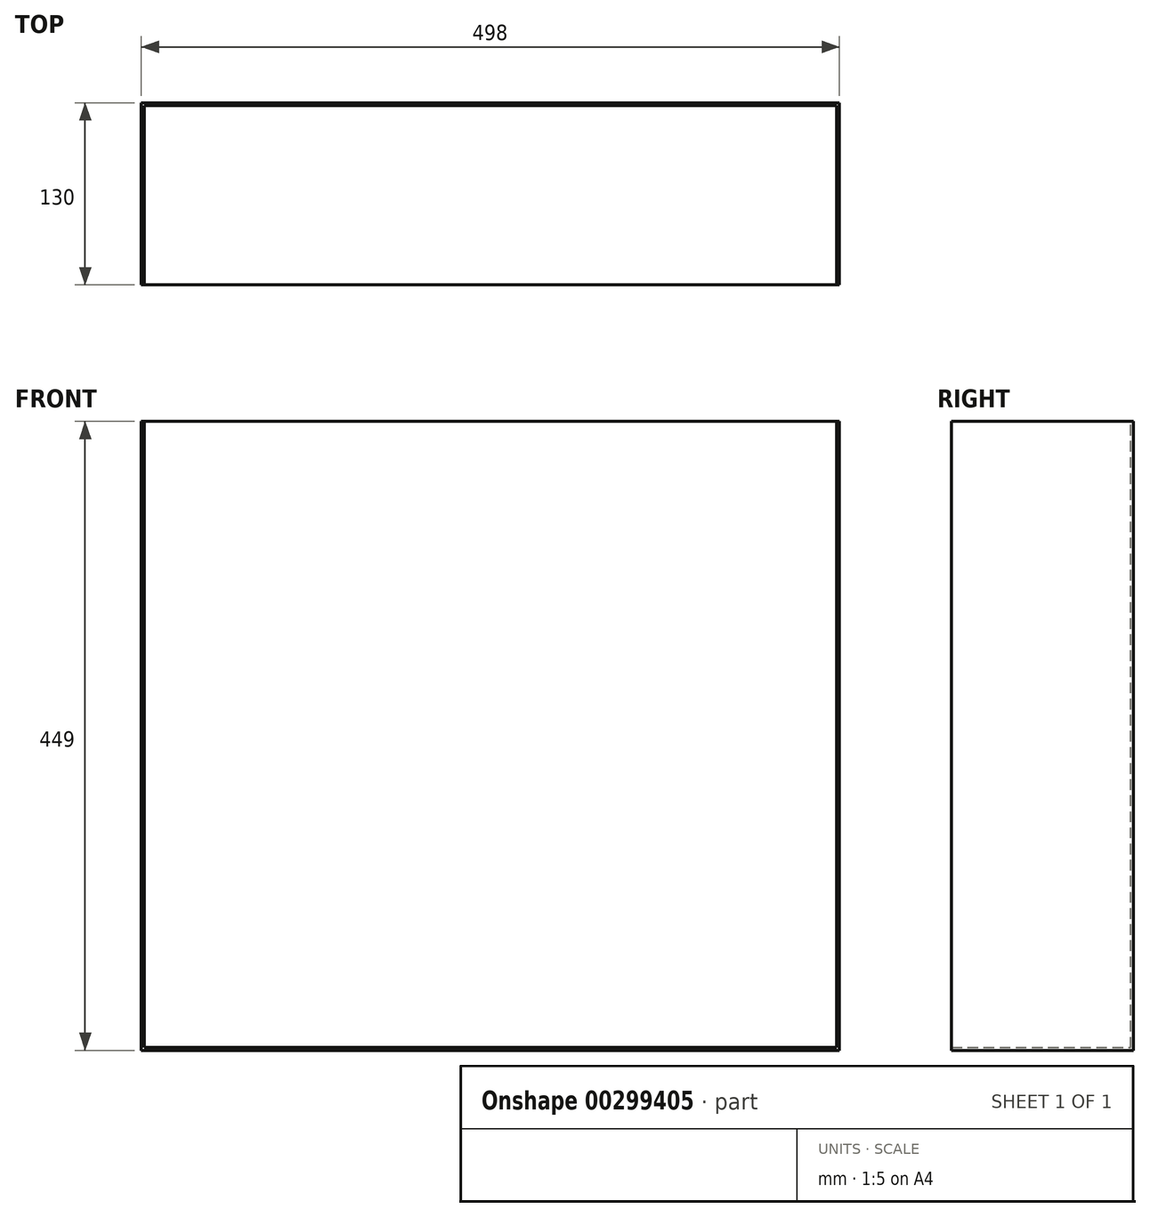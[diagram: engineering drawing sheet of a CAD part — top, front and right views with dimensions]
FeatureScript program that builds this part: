
annotation { "Feature Type Name" : "Feature", "Feature Type Description" : "" }
export const myFeature = defineFeature(function(context is Context, id is Id, definition is map)
    precondition{}
    {
        {
            var Q0;
            Q0=qCreatedBy(makeId("Top.planeOp"),FACE);
            var sketch = newSketch(context, id + "F0", { "sketchPlane" : qUnion([Q0])});
            skLineSegment(sketch, "E0.bottom", {"start": v(0, 0) * mm, "end": v(498, 0) * mm});
            skLineSegment(sketch, "E0.top", {"start": v(0, 130) * mm, "end": v(498, 130) * mm});
            skLineSegment(sketch, "E0.left", {"start": v(0, 0) * mm, "end": v(0, 130) * mm});
            skLineSegment(sketch, "E0.right", {"start": v(498, 0) * mm, "end": v(498, 130) * mm});
            skSolve(sketch);
        }
        {
            var Q0;
            Q0 = qSketchRegion(id + "F0", true);
            extrude(context, id + "F1", {"entities" : qUnion([Q0]), "oppositeDirection" : true, "depth" : 449 * mm});
        }
        {
            var Q0;
            Q0=makeQuery(id+"F1.opExtrude","SWEPT_FACE",FACE,{"disambiguationData":[OSD([sQuery(id+"F0.wireOp",EDGE,"E0.bottom")])]});
            var Q1;
            Q1=makeQuery(id+"F1.opExtrude","CAP_FACE",FACE,{"disambiguationData":[OSD([sQuery(id+"F0.wireOp",EDGE,"E0.bottom"),sQuery(id+"F0.wireOp",EDGE,"E0.top"),sQuery(id+"F0.wireOp",EDGE,"E0.left"),sQuery(id+"F0.wireOp",EDGE,"E0.right")])],"isStart":true});
            shell(context, id + "F2", {"entities" : qUnion([Q0, Q1]), "thickness" : 2 * mm});
        }
    });
